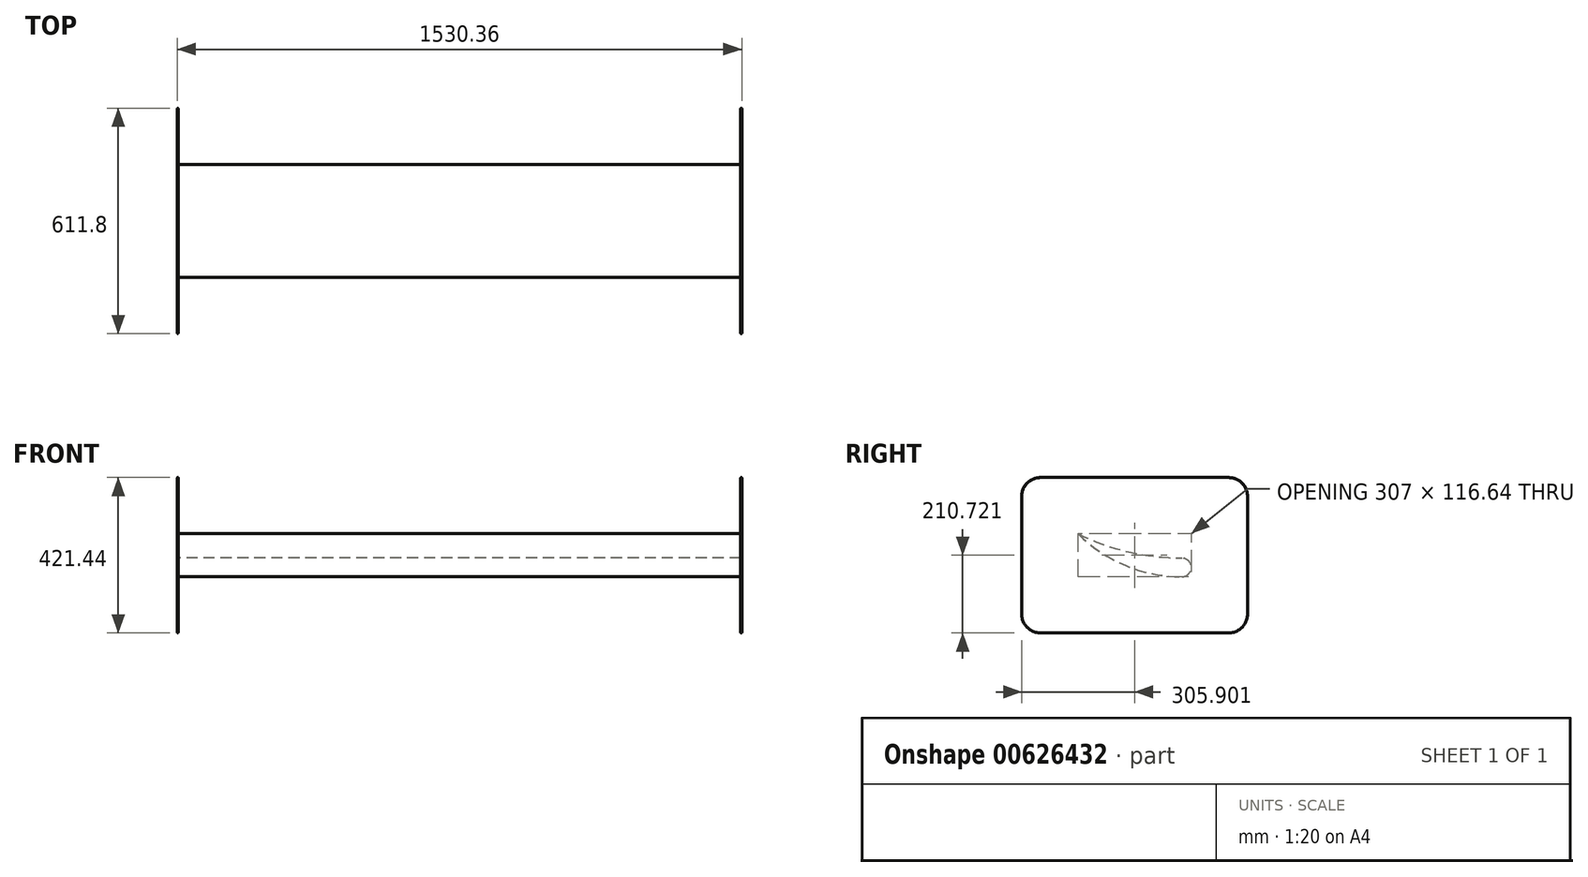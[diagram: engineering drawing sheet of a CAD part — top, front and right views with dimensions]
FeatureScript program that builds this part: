
annotation { "Feature Type Name" : "Feature", "Feature Type Description" : "" }
export const myFeature = defineFeature(function(context is Context, id is Id, definition is map)
    precondition{}
    {
        {
            var Q0;
            Q0=qCreatedBy(makeId("Right.planeOp"),FACE);
            var sketch = newSketch(context, id + "F0", { "sketchPlane" : qUnion([Q0])});
            skArc(sketch, "E0", {"start": v(0, -398.24) * mm, "mid": v(152.4, -367.93) * mm, "end": v(281.6, -281.6) * mm});
            skArc(sketch, "E1", {"start": v(0, -398.24) * mm, "mid": v(-25.4, -372.84) * mm, "end": v(0, -347.44) * mm});
            skArc(sketch, "E2", {"start": v(0, -347.44) * mm, "mid": v(144.6, -330.76) * mm, "end": v(281.6, -281.6) * mm});
            skLineSegment(sketch, "E3", {"start": v(0, 0) * mm, "end": v(281.6, -281.6) * mm});
            skSolve(sketch);
        }
        {
            var Q0;
            Q0 = qSketchRegion(id + "F0", true);
            extrude(context, id + "F1", {"entities" : qUnion([Q0]), "depth" : 762 * mm, "offsetDistance" : 25.4 * mm});
        }
        {
            var Q0;
            Q0=makeQuery(id+"F1.opExtrude","CAP_FACE",FACE,{"disambiguationData":[OSD([sQuery(id+"F0.wireOp",EDGE,"E0"),sQuery(id+"F0.wireOp",EDGE,"E1"),sQuery(id+"F0.wireOp",EDGE,"E2")])],"isStart":false});
            var sketch = newSketch(context, id + "F2", { "sketchPlane" : qUnion([Q0])});
            skLineSegment(sketch, "E4.bottom", {"start": v(-177.8, -129.2) * mm, "end": v(434, -129.2) * mm});
            skLineSegment(sketch, "E4.top", {"start": v(-177.8, -550.64) * mm, "end": v(434, -550.64) * mm});
            skLineSegment(sketch, "E4.left", {"start": v(-177.8, -129.2) * mm, "end": v(-177.8, -550.64) * mm});
            skLineSegment(sketch, "E4.right", {"start": v(434, -129.2) * mm, "end": v(434, -550.64) * mm});
            skSolve(sketch);
        }
        {
            var Q0;
            Q0 = qSketchRegion(id + "F2", true);
            extrude(context, id + "F3", {"entities" : qUnion([Q0]), "operationType" : NewBodyOperationType.ADD, "depth" : 3.17 * mm, "offsetDistance" : 25.4 * mm});
        }
        {
            var Q0;
            Q0=makeQuery(id+"F3.opExtrude","SWEPT_EDGE",EDGE,{"disambiguationData":[OSD([sQuery(id+"F2.wireOp",EDGE,"E4.bottom"),sQuery(id+"F2.wireOp",EDGE,"E4.left")])]});
            var Q1;
            Q1=makeQuery(id+"F3.opExtrude","SWEPT_EDGE",EDGE,{"disambiguationData":[OSD([sQuery(id+"F2.wireOp",EDGE,"E4.top"),sQuery(id+"F2.wireOp",EDGE,"E4.left")])]});
            var Q2;
            Q2=makeQuery(id+"F3.opExtrude","SWEPT_EDGE",EDGE,{"disambiguationData":[OSD([sQuery(id+"F2.wireOp",EDGE,"E4.bottom"),sQuery(id+"F2.wireOp",EDGE,"E4.right")])]});
            var Q3;
            Q3=makeQuery(id+"F3.opExtrude","SWEPT_EDGE",EDGE,{"disambiguationData":[OSD([sQuery(id+"F2.wireOp",EDGE,"E4.top"),sQuery(id+"F2.wireOp",EDGE,"E4.right")])]});
            fillet(context, id + "F4", {"entities" : qUnion([Q0, Q1, Q2, Q3]), "radius" : 50.8 * mm, "tangentPropagation" : true, "allowEdgeOverflow" : false});
        }
        {
            var Q0;
            Q0=makeQuery(id+"F3.opExtrude","CAP_EDGE",EDGE,{"disambiguationData":[OSD([sQuery(id+"F2.wireOp",EDGE,"E4.bottom")])],"isStart":false});
            var Q1;
            Q1=makeQuery(id+"F3.opExtrude","CAP_EDGE",EDGE,{"disambiguationData":[OSD([sQuery(id+"F2.wireOp",EDGE,"E4.bottom")])],"isStart":true});
            var Q2;
            Q2=makeQuery(id+"F3.opExtrude","CAP_EDGE",EDGE,{"disambiguationData":[OSD([sQuery(id+"F2.wireOp",EDGE,"E4.left")])],"isStart":false});
            var Q3;
            Q3=makeQuery(id+"F3.opExtrude","CAP_EDGE",EDGE,{"disambiguationData":[OSD([sQuery(id+"F2.wireOp",EDGE,"E4.left")])],"isStart":true});
            var Q4;
            {var subQ0=sQuery(id+"F2.wireOp",EDGE,"E4.left");var subQ1=sQuery(id+"F2.wireOp",EDGE,"E4.bottom");Q4=makeQuery(id+"F4.opFillet","BLEND_EDGE",EDGE,{"blendedFrom":[makeQuery(id+"F3.opExtrude","SWEPT_EDGE",EDGE,{"disambiguationData":[OSD([subQ1,subQ0])]}),makeQuery(id+"F3.opExtrude","CAP_FACE",FACE,{"disambiguationData":[OSD([subQ1,sQuery(id+"F2.wireOp",EDGE,"E4.top"),subQ0,sQuery(id+"F2.wireOp",EDGE,"E4.right")])],"isStart":false})],"blendedInto":[makeQuery(id+"F3.opExtrude","CAP_FACE",FACE,{"disambiguationData":[OSD([subQ1,sQuery(id+"F2.wireOp",EDGE,"E4.top"),subQ0,sQuery(id+"F2.wireOp",EDGE,"E4.right")])],"isStart":false})]});}
            var Q5;
            {var subQ0=sQuery(id+"F2.wireOp",EDGE,"E4.left");var subQ1=sQuery(id+"F2.wireOp",EDGE,"E4.bottom");Q5=makeQuery(id+"F4.opFillet","BLEND_EDGE",EDGE,{"blendedFrom":[makeQuery(id+"F3.opExtrude","SWEPT_EDGE",EDGE,{"disambiguationData":[OSD([subQ1,subQ0])]}),makeQuery(id+"F3.opExtrude","CAP_FACE",FACE,{"disambiguationData":[OSD([subQ1,sQuery(id+"F2.wireOp",EDGE,"E4.top"),subQ0,sQuery(id+"F2.wireOp",EDGE,"E4.right")])],"isStart":true})],"blendedInto":[makeQuery(id+"F3.opExtrude","CAP_FACE",FACE,{"disambiguationData":[OSD([subQ1,sQuery(id+"F2.wireOp",EDGE,"E4.top"),subQ0,sQuery(id+"F2.wireOp",EDGE,"E4.right")])],"isStart":true})]});}
            var Q6;
            {var subQ0=sQuery(id+"F2.wireOp",EDGE,"E4.left");var subQ1=sQuery(id+"F2.wireOp",EDGE,"E4.top");Q6=makeQuery(id+"F4.opFillet","BLEND_EDGE",EDGE,{"blendedFrom":[makeQuery(id+"F3.opExtrude","SWEPT_EDGE",EDGE,{"disambiguationData":[OSD([subQ1,subQ0])]}),makeQuery(id+"F3.opExtrude","CAP_FACE",FACE,{"disambiguationData":[OSD([sQuery(id+"F2.wireOp",EDGE,"E4.bottom"),subQ1,subQ0,sQuery(id+"F2.wireOp",EDGE,"E4.right")])],"isStart":false})],"blendedInto":[makeQuery(id+"F3.opExtrude","CAP_FACE",FACE,{"disambiguationData":[OSD([sQuery(id+"F2.wireOp",EDGE,"E4.bottom"),subQ1,subQ0,sQuery(id+"F2.wireOp",EDGE,"E4.right")])],"isStart":false})]});}
            var Q7;
            {var subQ0=sQuery(id+"F2.wireOp",EDGE,"E4.left");var subQ1=sQuery(id+"F2.wireOp",EDGE,"E4.top");Q7=makeQuery(id+"F4.opFillet","BLEND_EDGE",EDGE,{"blendedFrom":[makeQuery(id+"F3.opExtrude","SWEPT_EDGE",EDGE,{"disambiguationData":[OSD([subQ1,subQ0])]}),makeQuery(id+"F3.opExtrude","CAP_FACE",FACE,{"disambiguationData":[OSD([sQuery(id+"F2.wireOp",EDGE,"E4.bottom"),subQ1,subQ0,sQuery(id+"F2.wireOp",EDGE,"E4.right")])],"isStart":true})],"blendedInto":[makeQuery(id+"F3.opExtrude","CAP_FACE",FACE,{"disambiguationData":[OSD([sQuery(id+"F2.wireOp",EDGE,"E4.bottom"),subQ1,subQ0,sQuery(id+"F2.wireOp",EDGE,"E4.right")])],"isStart":true})]});}
            var Q8;
            Q8=makeQuery(id+"F3.opExtrude","CAP_EDGE",EDGE,{"disambiguationData":[OSD([sQuery(id+"F2.wireOp",EDGE,"E4.top")])],"isStart":true});
            var Q9;
            Q9=makeQuery(id+"F3.opExtrude","CAP_EDGE",EDGE,{"disambiguationData":[OSD([sQuery(id+"F2.wireOp",EDGE,"E4.top")])],"isStart":false});
            var Q10;
            {var subQ0=sQuery(id+"F2.wireOp",EDGE,"E4.right");var subQ1=sQuery(id+"F2.wireOp",EDGE,"E4.bottom");Q10=makeQuery(id+"F4.opFillet","BLEND_EDGE",EDGE,{"blendedFrom":[makeQuery(id+"F3.opExtrude","SWEPT_EDGE",EDGE,{"disambiguationData":[OSD([subQ1,subQ0])]}),makeQuery(id+"F3.opExtrude","CAP_FACE",FACE,{"disambiguationData":[OSD([subQ1,sQuery(id+"F2.wireOp",EDGE,"E4.top"),sQuery(id+"F2.wireOp",EDGE,"E4.left"),subQ0])],"isStart":false})],"blendedInto":[makeQuery(id+"F3.opExtrude","CAP_FACE",FACE,{"disambiguationData":[OSD([subQ1,sQuery(id+"F2.wireOp",EDGE,"E4.top"),sQuery(id+"F2.wireOp",EDGE,"E4.left"),subQ0])],"isStart":false})]});}
            var Q11;
            {var subQ0=sQuery(id+"F2.wireOp",EDGE,"E4.right");var subQ1=sQuery(id+"F2.wireOp",EDGE,"E4.bottom");Q11=makeQuery(id+"F4.opFillet","BLEND_EDGE",EDGE,{"blendedFrom":[makeQuery(id+"F3.opExtrude","SWEPT_EDGE",EDGE,{"disambiguationData":[OSD([subQ1,subQ0])]}),makeQuery(id+"F3.opExtrude","CAP_FACE",FACE,{"disambiguationData":[OSD([subQ1,sQuery(id+"F2.wireOp",EDGE,"E4.top"),sQuery(id+"F2.wireOp",EDGE,"E4.left"),subQ0])],"isStart":true})],"blendedInto":[makeQuery(id+"F3.opExtrude","CAP_FACE",FACE,{"disambiguationData":[OSD([subQ1,sQuery(id+"F2.wireOp",EDGE,"E4.top"),sQuery(id+"F2.wireOp",EDGE,"E4.left"),subQ0])],"isStart":true})]});}
            var Q12;
            Q12=makeQuery(id+"F3.opExtrude","CAP_EDGE",EDGE,{"disambiguationData":[OSD([sQuery(id+"F2.wireOp",EDGE,"E4.right")])],"isStart":false});
            var Q13;
            Q13=makeQuery(id+"F3.opExtrude","CAP_EDGE",EDGE,{"disambiguationData":[OSD([sQuery(id+"F2.wireOp",EDGE,"E4.right")])],"isStart":true});
            var Q14;
            {var subQ0=sQuery(id+"F2.wireOp",EDGE,"E4.right");var subQ1=sQuery(id+"F2.wireOp",EDGE,"E4.top");Q14=makeQuery(id+"F4.opFillet","BLEND_EDGE",EDGE,{"blendedFrom":[makeQuery(id+"F3.opExtrude","SWEPT_EDGE",EDGE,{"disambiguationData":[OSD([subQ1,subQ0])]}),makeQuery(id+"F3.opExtrude","CAP_FACE",FACE,{"disambiguationData":[OSD([sQuery(id+"F2.wireOp",EDGE,"E4.bottom"),subQ1,sQuery(id+"F2.wireOp",EDGE,"E4.left"),subQ0])],"isStart":false})],"blendedInto":[makeQuery(id+"F3.opExtrude","CAP_FACE",FACE,{"disambiguationData":[OSD([sQuery(id+"F2.wireOp",EDGE,"E4.bottom"),subQ1,sQuery(id+"F2.wireOp",EDGE,"E4.left"),subQ0])],"isStart":false})]});}
            var Q15;
            {var subQ0=sQuery(id+"F2.wireOp",EDGE,"E4.right");var subQ1=sQuery(id+"F2.wireOp",EDGE,"E4.top");Q15=makeQuery(id+"F4.opFillet","BLEND_EDGE",EDGE,{"blendedFrom":[makeQuery(id+"F3.opExtrude","SWEPT_EDGE",EDGE,{"disambiguationData":[OSD([subQ1,subQ0])]}),makeQuery(id+"F3.opExtrude","CAP_FACE",FACE,{"disambiguationData":[OSD([sQuery(id+"F2.wireOp",EDGE,"E4.bottom"),subQ1,sQuery(id+"F2.wireOp",EDGE,"E4.left"),subQ0])],"isStart":true})],"blendedInto":[makeQuery(id+"F3.opExtrude","CAP_FACE",FACE,{"disambiguationData":[OSD([sQuery(id+"F2.wireOp",EDGE,"E4.bottom"),subQ1,sQuery(id+"F2.wireOp",EDGE,"E4.left"),subQ0])],"isStart":true})]});}
            fillet(context, id + "F5", {"entities" : qUnion([Q0, Q1, Q2, Q3, Q4, Q5, Q6, Q7, Q8, Q9, Q10, Q11, Q12, Q13, Q14, Q15]), "radius" : 1.59 * mm, "tangentPropagation" : true, "allowEdgeOverflow" : false});
        }
        {
            var Q0;
            Q0=makeQuery(id+"F1.opExtrude","SWEPT_BODY",BODY,{"disambiguationData":[OSD([sQuery(id+"F0.wireOp",EDGE,"E0"),sQuery(id+"F0.wireOp",EDGE,"E1"),sQuery(id+"F0.wireOp",EDGE,"E2")])]});
            var Q1;
            Q1=makeQuery(id+"F1.opExtrude","CAP_FACE",FACE,{"disambiguationData":[OSD([sQuery(id+"F0.wireOp",EDGE,"E0"),sQuery(id+"F0.wireOp",EDGE,"E1"),sQuery(id+"F0.wireOp",EDGE,"E2")])],"isStart":true});
            mirror(context, id + "F6", {"operationType" : NewBodyOperationType.ADD, "entities" : qUnion([Q0]), "mirrorPlane" : qUnion([Q1])});
        }
        {
            var Q0;
            Q0=makeQuery(id+"F1.opExtrude","SWEPT_BODY",BODY,{"disambiguationData":[OSD([sQuery(id+"F0.wireOp",EDGE,"E0"),sQuery(id+"F0.wireOp",EDGE,"E1"),sQuery(id+"F0.wireOp",EDGE,"E2")])]});
            var Q1;
            Q1=qCreatedBy(makeId("Front.planeOp"),FACE);
            mirror(context, id + "F7", {"entities" : qUnion([Q0]), "mirrorPlane" : qUnion([Q1])});
        }
        {
            var Q0;
            Q0=makeQuery(id+"F1.opExtrude","SWEPT_BODY",BODY,{"disambiguationData":[OSD([sQuery(id+"F0.wireOp",EDGE,"E0"),sQuery(id+"F0.wireOp",EDGE,"E1"),sQuery(id+"F0.wireOp",EDGE,"E2")])]});
            deleteBodies(context, id + "F8", {"entities" : qUnion([Q0])});
        }
    });
